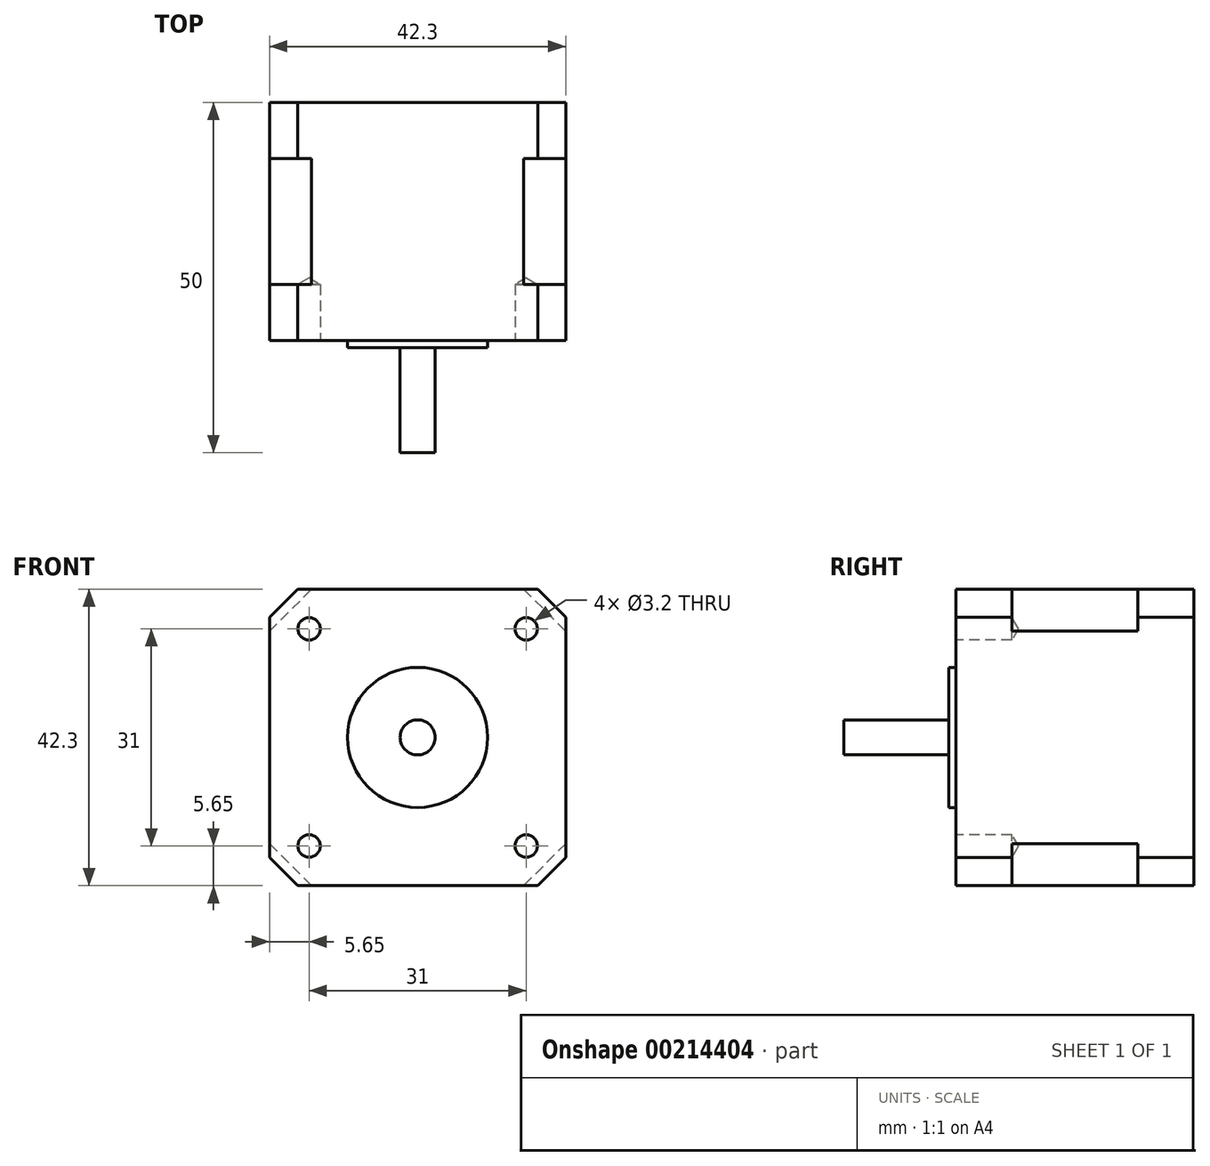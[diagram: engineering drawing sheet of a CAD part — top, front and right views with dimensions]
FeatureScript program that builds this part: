
annotation { "Feature Type Name" : "Feature", "Feature Type Description" : "" }
export const myFeature = defineFeature(function(context is Context, id is Id, definition is map)
    precondition{}
    {
        {
            var Q0;
            Q0=qCreatedBy(makeId("Front.planeOp"),FACE);
            var sketch = newSketch(context, id + "F0", { "sketchPlane" : qUnion([Q0])});
            skLineSegment(sketch, "E0.bottom", {"start": v(-17.15, -21.15) * mm, "end": v(17.15, -21.15) * mm});
            skLineSegment(sketch, "E0.top", {"start": v(-17.15, 21.15) * mm, "end": v(17.15, 21.15) * mm});
            skLineSegment(sketch, "E0.left", {"start": v(-21.15, -17.15) * mm, "end": v(-21.15, 17.15) * mm});
            skLineSegment(sketch, "E0.right", {"start": v(21.15, -17.15) * mm, "end": v(21.15, 17.15) * mm});
            skPoint(sketch, "E0.middle", {"position": v(0, 0) * mm});
            skLineSegment(sketch, "E1", {"start": v(17.15, 21.15) * mm, "end": v(21.15, 17.15) * mm});
            skLineSegment(sketch, "E2", {"start": v(-21.15, 17.15) * mm, "end": v(-17.15, 21.15) * mm});
            skLineSegment(sketch, "E3", {"start": v(-21.15, -17.15) * mm, "end": v(-17.15, -21.15) * mm});
            skLineSegment(sketch, "E4", {"start": v(17.15, -21.15) * mm, "end": v(21.15, -17.15) * mm});
            skPoint(sketch, "E5.orphan", {"position": v(-21.15, 21.15) * mm});
            skPoint(sketch, "E6.orphan", {"position": v(21.15, 21.15) * mm});
            skPoint(sketch, "E7.orphan", {"position": v(21.15, -21.15) * mm});
            skPoint(sketch, "E8.orphan", {"position": v(-21.15, -21.15) * mm});
            skSolve(sketch);
        }
        {
            var Q0;
            Q0 = qSketchRegion(id + "F0", true);
            extrude(context, id + "F1", {"entities" : qUnion([Q0]), "depth" : 8 * mm});
        }
        {
            var Q0;
            Q0=makeQuery(id+"F1.opExtrude","CAP_FACE",FACE,{"disambiguationData":[OSD([sQuery(id+"F0.wireOp",EDGE,"E0.bottom"),sQuery(id+"F0.wireOp",EDGE,"E0.top"),sQuery(id+"F0.wireOp",EDGE,"E0.left"),sQuery(id+"F0.wireOp",EDGE,"E0.right"),sQuery(id+"F0.wireOp",EDGE,"E1"),sQuery(id+"F0.wireOp",EDGE,"E2"),sQuery(id+"F0.wireOp",EDGE,"E3"),sQuery(id+"F0.wireOp",EDGE,"E4")])],"isStart":false});
            var sketch = newSketch(context, id + "F2", { "sketchPlane" : qUnion([Q0])});
            skLineSegment(sketch, "E9", {"start": v(-21.15, -15.15) * mm, "end": v(-21.15, 15.15) * mm});
            skLineSegment(sketch, "E10", {"start": v(-21.15, 15.15) * mm, "end": v(-15.15, 21.15) * mm});
            skLineSegment(sketch, "E11", {"start": v(-15.15, 21.15) * mm, "end": v(15.15, 21.15) * mm});
            skLineSegment(sketch, "E12", {"start": v(15.15, 21.15) * mm, "end": v(21.15, 15.15) * mm});
            skLineSegment(sketch, "E13", {"start": v(21.15, 15.15) * mm, "end": v(21.15, -15.15) * mm});
            skLineSegment(sketch, "E14", {"start": v(21.15, -15.15) * mm, "end": v(15.15, -21.15) * mm});
            skLineSegment(sketch, "E15", {"start": v(15.15, -21.15) * mm, "end": v(-15.15, -21.15) * mm});
            skLineSegment(sketch, "E16", {"start": v(-15.15, -21.15) * mm, "end": v(-21.15, -15.15) * mm});
            skSolve(sketch);
        }
        {
            var Q0;
            Q0 = qSketchRegion(id + "F2", true);
            extrude(context, id + "F3", {"entities" : qUnion([Q0]), "operationType" : NewBodyOperationType.ADD, "depth" : 18 * mm});
        }
        {
            var Q0;
            Q0=makeQuery(id+"F3.opExtrude","CAP_FACE",FACE,{"disambiguationData":[OSD([sQuery(id+"F2.wireOp",EDGE,"E9"),sQuery(id+"F2.wireOp",EDGE,"E10"),sQuery(id+"F2.wireOp",EDGE,"E11"),sQuery(id+"F2.wireOp",EDGE,"E12"),sQuery(id+"F2.wireOp",EDGE,"E13"),sQuery(id+"F2.wireOp",EDGE,"E14"),sQuery(id+"F2.wireOp",EDGE,"E15"),sQuery(id+"F2.wireOp",EDGE,"E16")])],"isStart":false});
            var sketch = newSketch(context, id + "F4", { "sketchPlane" : qUnion([Q0])});
            skLineSegment(sketch, "E17", {"start": v(-21.15, -17.15) * mm, "end": v(-21.15, 17.15) * mm});
            skLineSegment(sketch, "E18", {"start": v(-21.15, 17.15) * mm, "end": v(-17.15, 21.15) * mm});
            skLineSegment(sketch, "E19", {"start": v(-17.15, 21.15) * mm, "end": v(17.15, 21.15) * mm});
            skLineSegment(sketch, "E20", {"start": v(17.15, 21.15) * mm, "end": v(21.15, 17.15) * mm});
            skLineSegment(sketch, "E21", {"start": v(21.15, 17.15) * mm, "end": v(21.15, -17.15) * mm});
            skLineSegment(sketch, "E22", {"start": v(21.15, -17.15) * mm, "end": v(17.15, -21.15) * mm});
            skLineSegment(sketch, "E23", {"start": v(17.15, -21.15) * mm, "end": v(-17.15, -21.15) * mm});
            skLineSegment(sketch, "E24", {"start": v(-17.15, -21.15) * mm, "end": v(-21.15, -17.15) * mm});
            skSolve(sketch);
        }
        {
            var Q0;
            Q0 = qSketchRegion(id + "F4", true);
            extrude(context, id + "F5", {"entities" : qUnion([Q0]), "operationType" : NewBodyOperationType.ADD, "depth" : 8 * mm});
        }
        {
            var Q0;
            Q0=makeQuery(id+"F5.opExtrude","CAP_FACE",FACE,{"disambiguationData":[OSD([sQuery(id+"F4.wireOp",EDGE,"E17"),sQuery(id+"F4.wireOp",EDGE,"E18"),sQuery(id+"F4.wireOp",EDGE,"E19"),sQuery(id+"F4.wireOp",EDGE,"E20"),sQuery(id+"F4.wireOp",EDGE,"E21"),sQuery(id+"F4.wireOp",EDGE,"E22"),sQuery(id+"F4.wireOp",EDGE,"E23"),sQuery(id+"F4.wireOp",EDGE,"E24")])],"isStart":false});
            var sketch = newSketch(context, id + "F6", { "sketchPlane" : qUnion([Q0])});
            skCircle(sketch, "E25", {"center": v(0, 0) * mm, "radius": 10 * mm});
            skSolve(sketch);
        }
        {
            var Q0;
            Q0 = qSketchRegion(id + "F6", true);
            extrude(context, id + "F7", {"entities" : qUnion([Q0]), "operationType" : NewBodyOperationType.ADD, "depth" : 1 * mm});
        }
        {
            var Q0;
            Q0=makeQuery(id+"F5.opExtrude","CAP_FACE",FACE,{"disambiguationData":[OSD([sQuery(id+"F4.wireOp",EDGE,"E17"),sQuery(id+"F4.wireOp",EDGE,"E18"),sQuery(id+"F4.wireOp",EDGE,"E19"),sQuery(id+"F4.wireOp",EDGE,"E20"),sQuery(id+"F4.wireOp",EDGE,"E21"),sQuery(id+"F4.wireOp",EDGE,"E22"),sQuery(id+"F4.wireOp",EDGE,"E23"),sQuery(id+"F4.wireOp",EDGE,"E24")])],"isStart":false});
            var sketch = newSketch(context, id + "F8", { "sketchPlane" : qUnion([Q0])});
            skPoint(sketch, "E26", {"position": v(-15.5, 15.5) * mm});
            skPoint(sketch, "E27", {"position": v(15.5, 15.5) * mm});
            skPoint(sketch, "E28", {"position": v(15.5, -15.5) * mm});
            skPoint(sketch, "E29", {"position": v(-15.5, -15.5) * mm});
            skSolve(sketch);
        }
        {
            var Q0;
            Q0=sQuery(id+"F8.wireOp",VERTEX,"E26");
            var Q1;
            Q1=sQuery(id+"F8.wireOp",VERTEX,"E27");
            var Q2;
            Q2=sQuery(id+"F8.wireOp",VERTEX,"E28");
            var Q3;
            Q3=sQuery(id+"F8.wireOp",VERTEX,"E29");
            var Q4;
            Q4=makeQuery(id+"F1.opExtrude","SWEPT_BODY",BODY,{"disambiguationData":[OSD([sQuery(id+"F0.wireOp",EDGE,"E0.bottom"),sQuery(id+"F0.wireOp",EDGE,"E0.top"),sQuery(id+"F0.wireOp",EDGE,"E0.left"),sQuery(id+"F0.wireOp",EDGE,"E0.right"),sQuery(id+"F0.wireOp",EDGE,"E1"),sQuery(id+"F0.wireOp",EDGE,"E2"),sQuery(id+"F0.wireOp",EDGE,"E3"),sQuery(id+"F0.wireOp",EDGE,"E4")])]});
            hole(context, id + "F9", {"style" : HoleStyle.SIMPLE, "endStyle" : HoleEndStyle.BLIND, "standardTappedOrClearance" : lookupTablePath({ "standard" : "ISO", "engagement" : "75%", "pitch" : "0.75 mm", "size" : "M4", "type" : "Tapped" }), "standardBlindInLast" : lookupTablePath({ "standard" : "ISO", "engagement" : "75%", "pitch" : "0.75 mm", "size" : "M4", "type" : "Tapped" }), "holeDiameter" : 3.2 * mm, "holeDepth" : 8 * mm, "startFromSketch" : true, "locations" : qUnion([Q0, Q1, Q2, Q3]), "scope" : qUnion([Q4])});
        }
        {
            var Q0;
            Q0=makeQuery(id+"F7.opExtrude","CAP_FACE",FACE,{"disambiguationData":[OSD([sQuery(id+"F6.wireOp",EDGE,"E25")])],"isStart":false});
            var sketch = newSketch(context, id + "F10", { "sketchPlane" : qUnion([Q0])});
            skCircle(sketch, "E30", {"center": v(0, 0) * mm, "radius": 2.5 * mm});
            skSolve(sketch);
        }
        {
            var Q0;
            Q0 = qSketchRegion(id + "F10", true);
            extrude(context, id + "F11", {"entities" : qUnion([Q0]), "operationType" : NewBodyOperationType.ADD, "depth" : 15 * mm});
        }
    });
